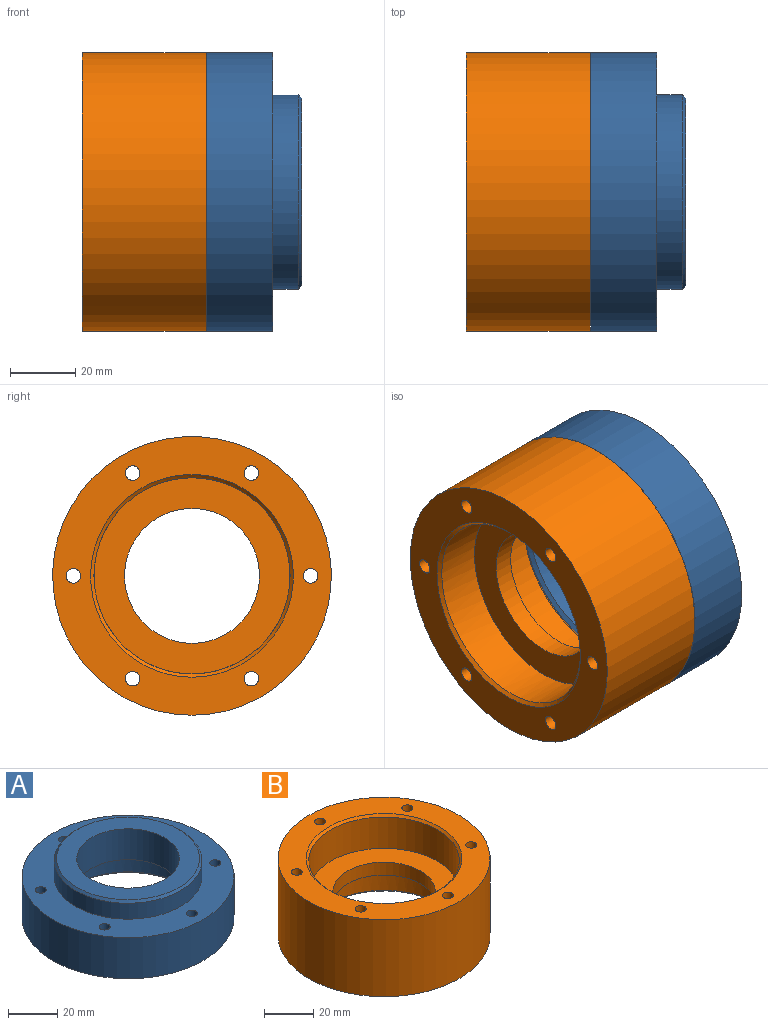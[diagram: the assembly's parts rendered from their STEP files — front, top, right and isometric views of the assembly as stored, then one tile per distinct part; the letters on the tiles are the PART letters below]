
ASSEMBLY  parts=2 mates=1
PART A: 16 faces, bbox 85.7x85.7x29.2 mm
  f0: plane 60.96x60.96mm, normal (0,0,-1), area 1565.7mm2, adj f4,f5
  f1: cylinder r=42.86mm len=85.73mm, axis (0,0,-1), area 5472.4mm2, adj f2,f3
  f2: plane 85.73x85.73mm, normal (0,0,1), area 2866.3mm2, adj f1,f6,f10,f11,f12,f13,f14,f15
  f3: plane 85.73x85.73mm, normal (0,0,-1), area 2560mm2, adj f1,f8,f10,f11,f12,f13,f14,f15
  f4: cylinder r=20.75mm len=41.5mm, axis (0,0,1), area 1987.1mm2, adj f0,f7
  f5: cylinder r=30.48mm len=60.96mm, axis (0,0,-1), area 2480.8mm2, adj f0,f8
  f6: cylinder r=29.91mm len=59.82mm, axis (0,0,-1), area 1479.7mm2, adj f2,f9
  f7: plane 57.79x57.79mm, normal (0,0,1), area 1269.6mm2, adj f4,f9
  f8: cone r=30.48mm half-angle=45deg, axis (0,0,-1), area 279.8mm2, adj f3,f5
  f9: cone r=28.89mm half-angle=45deg, axis (0,0,-1), area 265.4mm2, adj f6,f7
  f10: cylinder r=2.25mm len=20.32mm, axis (0,0,1), area 287mm2, adj f2,f3
  f11: cylinder r=2.25mm len=20.32mm, axis (0,0,1), area 287mm2, adj f2,f3
  f12: cylinder r=2.25mm len=20.32mm, axis (0,0,1), area 287mm2, adj f2,f3
  f13: cylinder r=2.25mm len=20.32mm, axis (0,0,1), area 287mm2, adj f2,f3
  f14: cylinder r=2.25mm len=20.32mm, axis (0,0,1), area 287mm2, adj f2,f3
  f15: cylinder r=2.25mm len=20.32mm, axis (0,0,1), area 287mm2, adj f2,f3
PART B: 16 faces, bbox 85.7x85.7x38.1 mm
  f0: cylinder r=20.75mm len=41.5mm, axis (0,0,1), area 828mm2, adj f1,f7
  f1: plane 60.96x60.96mm, normal (0,0,1), area 1565.7mm2, adj f0,f5
  f2: cylinder r=42.86mm len=85.73mm, axis (0,0,-1), area 10260.8mm2, adj f3,f4
  f3: plane 85.73x85.73mm, normal (0,0,1), area 2560mm2, adj f2,f9,f10,f11,f12,f13,f14,f15
  f4: plane 85.73x85.73mm, normal (0,0,-1), area 2622.5mm2, adj f2,f8,f10,f11,f12,f13,f14,f15
  f5: cylinder r=30.48mm len=60.96mm, axis (0,0,1), area 2967.3mm2, adj f1,f9
  f6: cylinder r=30.16mm len=60.33mm, axis (0,0,-1), area 2695.7mm2, adj f7,f8
  f7: plane 60.33x60.33mm, normal (0,0,-1), area 1505.3mm2, adj f0,f6
  f8: cone r=30.16mm half-angle=45deg, axis (0,0,-1), area 276.9mm2, adj f4,f6
  f9: cone r=30.48mm half-angle=45deg, axis (0,0,1), area 279.8mm2, adj f3,f5
  f10: cylinder r=2.25mm len=38.1mm, axis (0,0,1), area 538.1mm2, adj f3,f4
  f11: cylinder r=2.25mm len=38.1mm, axis (0,0,1), area 538.1mm2, adj f3,f4
  f12: cylinder r=2.25mm len=38.1mm, axis (0,0,1), area 538.1mm2, adj f3,f4
  f13: cylinder r=2.25mm len=38.1mm, axis (0,0,1), area 538.1mm2, adj f3,f4
  f14: cylinder r=2.25mm len=38.1mm, axis (0,0,1), area 538.1mm2, adj f3,f4
  f15: cylinder r=2.25mm len=38.1mm, axis (0,0,1), area 538.1mm2, adj f3,f4
PLACE A rot(axis=(0,1,0),90deg) t=(16.92,26.72,-82.14)mm
PLACE B rot(axis=(0,1,0),90deg) t=(-21.27,26.72,-82.14)mm
MATE slider A.f6 <-> B.f6  axis (1,0,0) through (46.13,26.72,-82.14)mm
